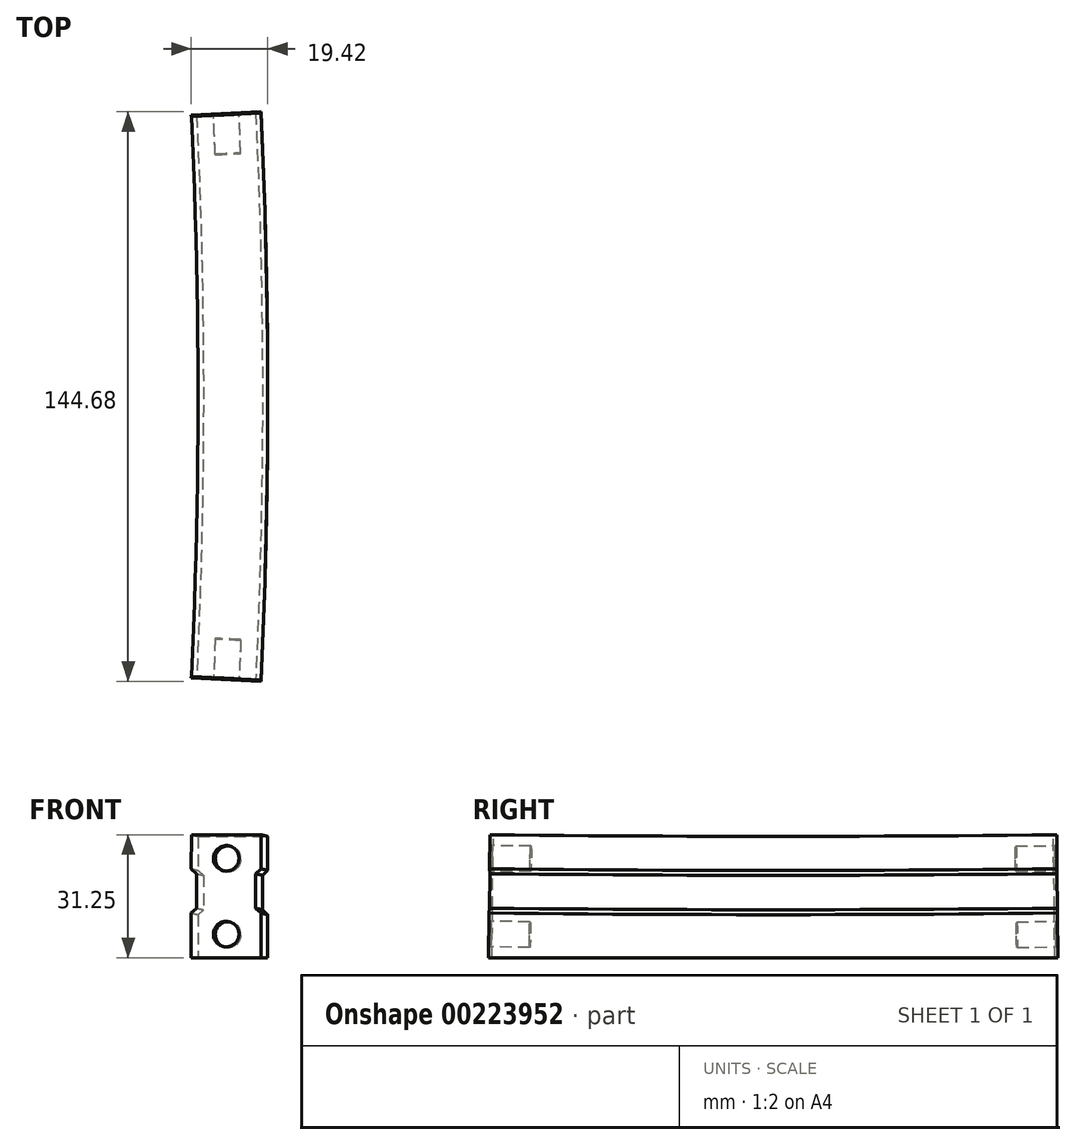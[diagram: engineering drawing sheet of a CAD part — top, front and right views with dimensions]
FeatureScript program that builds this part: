
annotation { "Feature Type Name" : "Feature", "Feature Type Description" : "" }
export const myFeature = defineFeature(function(context is Context, id is Id, definition is map)
    precondition{}
    {
        {
            var Q0;
            Q0=qCreatedBy(makeId("Front.planeOp"),FACE);
            var sketch = newSketch(context, id + "F0", { "sketchPlane" : qUnion([Q0])});
            skLineSegment(sketch, "E0.bottom", {"start": v(0, 0) * mm, "end": v(17.7, 0) * mm, "construction": true});
            skLineSegment(sketch, "E0.top", {"start": v(0, 31.25) * mm, "end": v(17.7, 31.25) * mm, "construction": true});
            skLineSegment(sketch, "E0.left", {"start": v(0, 0) * mm, "end": v(0, 31.25) * mm, "construction": true});
            skLineSegment(sketch, "E0.right", {"start": v(17.7, 0) * mm, "end": v(17.7, 31.25) * mm, "construction": true});
            skLineSegment(sketch, "E1", {"start": v(8.85, 31.25) * mm, "end": v(8.85, 0) * mm, "construction": true});
            skLineSegment(sketch, "E2", {"start": v(8.85, 0) * mm, "end": v(0, 0) * mm});
            skLineSegment(sketch, "E3", {"start": v(0, 11.35) * mm, "end": v(1.35, 12.6) * mm});
            skLineSegment(sketch, "E4", {"start": v(1.35, 12.6) * mm, "end": v(1.35, 21.35) * mm});
            skLineSegment(sketch, "E5", {"start": v(1.35, 21.35) * mm, "end": v(0, 22.6) * mm});
            skLineSegment(sketch, "E6", {"start": v(0, 22.6) * mm, "end": v(0, 31.25) * mm});
            skLineSegment(sketch, "E7", {"start": v(8.85, 31.25) * mm, "end": v(0, 31.25) * mm});
            skLineSegment(sketch, "E8", {"start": v(0, 0) * mm, "end": v(0, 11.35) * mm});
            skLineSegment(sketch, "E9.MirrorCS", {"start": v(16.35, 21.35) * mm, "end": v(17.7, 22.6) * mm});
            skLineSegment(sketch, "E10.MirrorCS", {"start": v(17.7, 11.35) * mm, "end": v(16.35, 12.6) * mm});
            skLineSegment(sketch, "E11.MirrorCS", {"start": v(17.7, 0) * mm, "end": v(17.7, 11.35) * mm});
            skLineSegment(sketch, "E12.MirrorCS", {"start": v(8.85, 31.25) * mm, "end": v(17.7, 31.25) * mm});
            skLineSegment(sketch, "E13.MirrorCS", {"start": v(8.85, 0) * mm, "end": v(17.7, 0) * mm});
            skLineSegment(sketch, "E14.MirrorCS", {"start": v(16.35, 12.6) * mm, "end": v(16.35, 21.35) * mm});
            skLineSegment(sketch, "E15.MirrorCS", {"start": v(17.7, 22.6) * mm, "end": v(17.7, 31.25) * mm});
            skLineSegment(sketch, "E16", {"start": v(0, 11.35) * mm, "end": v(1.35, 11.35) * mm, "construction": true});
            skLineSegment(sketch, "E17", {"start": v(1.35, 11.35) * mm, "end": v(1.35, 12.6) * mm, "construction": true});
            skLineSegment(sketch, "E18", {"start": v(0, 22.6) * mm, "end": v(1.35, 22.6) * mm, "construction": true});
            skLineSegment(sketch, "E19", {"start": v(1.35, 22.6) * mm, "end": v(1.35, 21.35) * mm, "construction": true});
            skPoint(sketch, "E20", {"position": v(17.7, 0) * mm});
            skLineSegment(sketch, "E21", {"start": v(0.24, 33.32) * mm, "end": v(17.46, 29.18) * mm, "construction": true});
            skSolve(sketch);
        }
        {
            var Q0;
            Q0=qCreatedBy(makeId("Top.planeOp"),FACE);
            var Q1;
            Q1=sQuery(id+"F0.wireOp",EDGE,"E21");
            cPlane(context, id + "F1", {"entities" : qUnion([Q0, Q1]), "cplaneType" : CPlaneType.LINE_ANGLE, "offset" : 25 * mm, "angle" : 0 * degree, "width" : 150 * mm, "height" : 150 * mm});
        }
        {
            var Q0;
            Q0=qCreatedBy(id+"F1.planeOp",FACE);
            var sketch = newSketch(context, id + "F2", { "sketchPlane" : qUnion([Q0])});
            skArc(sketch, "E22", {"start": v(1.31, 0) * mm, "mid": v(0.88, 35.79) * mm, "end": v(-0.44, 71.56) * mm});
            skArc(sketch, "E23", {"start": v(1.31, 0) * mm, "mid": v(0.88, -35.79) * mm, "end": v(-0.44, -71.56) * mm});
            skLineSegment(sketch, "E24", {"start": v(-1457.02, 0) * mm, "end": v(1.31, 0) * mm, "construction": true});
            skLineSegment(sketch, "E25", {"start": v(-0.44, 71.56) * mm, "end": v(-1457.02, 0) * mm, "construction": true});
            skLineSegment(sketch, "E26", {"start": v(-0.44, -71.56) * mm, "end": v(-1457.02, 0) * mm, "construction": true});
            skSolve(sketch);
        }
        {
            var Q0;
            Q0 = qSketchRegion(id + "F0", true);
            var Q1;
            Q1=sQuery(id+"F2.wireOp",EDGE,"E22");
            sweep(context, id + "F3", {"profiles" : qUnion([Q0]), "path" : qUnion([Q1])});
        }
        {
            var Q0;
            Q0 = qSketchRegion(id + "F0", true);
            var Q1;
            Q1=sQuery(id+"F2.wireOp",EDGE,"E23");
            sweep(context, id + "F4", {"operationType" : NewBodyOperationType.ADD, "profiles" : qUnion([Q0]), "path" : qUnion([Q1])});
        }
        {
            var Q0;
            Q0=makeQuery(id+"F3.opSweep","CAP_FACE",FACE,{"disambiguationData":[OSD([sQuery(id+"F0.wireOp",EDGE,"E2"),sQuery(id+"F0.wireOp",EDGE,"E3"),sQuery(id+"F0.wireOp",EDGE,"E4"),sQuery(id+"F0.wireOp",EDGE,"E5"),sQuery(id+"F0.wireOp",EDGE,"E6"),sQuery(id+"F0.wireOp",EDGE,"E7"),sQuery(id+"F0.wireOp",EDGE,"E8"),sQuery(id+"F0.wireOp",EDGE,"E9.MirrorCS"),sQuery(id+"F0.wireOp",EDGE,"E10.MirrorCS"),sQuery(id+"F0.wireOp",EDGE,"E11.MirrorCS"),sQuery(id+"F0.wireOp",EDGE,"E12.MirrorCS"),sQuery(id+"F0.wireOp",EDGE,"E13.MirrorCS"),sQuery(id+"F0.wireOp",EDGE,"E14.MirrorCS"),sQuery(id+"F0.wireOp",EDGE,"E15.MirrorCS"),sQuery(id+"F2.wireOp",VERTEX,"E22.end")])],"isStart":false});
            var sketch = newSketch(context, id + "F5", { "sketchPlane" : qUnion([Q0])});
            skLineSegment(sketch, "E27.bottom", {"start": v(1.71, 30.84) * mm, "end": v(19.42, 30.84) * mm, "construction": true});
            skLineSegment(sketch, "E27.top", {"start": v(1.71, -0.41) * mm, "end": v(19.42, -0.41) * mm, "construction": true});
            skLineSegment(sketch, "E27.left", {"start": v(1.71, 30.84) * mm, "end": v(1.71, -0.41) * mm, "construction": true});
            skLineSegment(sketch, "E27.right", {"start": v(19.42, 30.84) * mm, "end": v(19.42, -0.41) * mm, "construction": true});
            skLineSegment(sketch, "E28", {"start": v(10.57, 30.84) * mm, "end": v(10.57, -0.41) * mm, "construction": true});
            skCircle(sketch, "E29", {"center": v(10.57, 5.59) * mm, "radius": 3.25 * mm});
            skCircle(sketch, "E30", {"center": v(10.57, 24.84) * mm, "radius": 3.25 * mm});
            skSolve(sketch);
        }
        {
            var Q0;
            Q0=makeQuery(id+"F5.imprint","IMPRINT",FACE,{"disambiguationData":[TD([[makeQuery(id+"F5.imprint","IMPRINT",EDGE,{"derivedFrom":sQuery(id+"F5.wireOp",EDGE,"E30")}),1.0]])]});
            var Q1;
            Q1=makeQuery(id+"F5.imprint","IMPRINT",FACE,{"disambiguationData":[TD([[makeQuery(id+"F5.imprint","IMPRINT",EDGE,{"derivedFrom":sQuery(id+"F5.wireOp",EDGE,"E29")}),1.0]])]});
            extrude(context, id + "F6", {"entities" : qUnion([Q0, Q1]), "operationType" : NewBodyOperationType.REMOVE, "oppositeDirection" : true, "depth" : 10 * mm});
        }
        {
            var Q0;
            Q0=makeQuery(id+"F4.opSweep","CAP_FACE",FACE,{"disambiguationData":[OSD([sQuery(id+"F0.wireOp",EDGE,"E2"),sQuery(id+"F0.wireOp",EDGE,"E3"),sQuery(id+"F0.wireOp",EDGE,"E4"),sQuery(id+"F0.wireOp",EDGE,"E5"),sQuery(id+"F0.wireOp",EDGE,"E6"),sQuery(id+"F0.wireOp",EDGE,"E7"),sQuery(id+"F0.wireOp",EDGE,"E8"),sQuery(id+"F0.wireOp",EDGE,"E9.MirrorCS"),sQuery(id+"F0.wireOp",EDGE,"E10.MirrorCS"),sQuery(id+"F0.wireOp",EDGE,"E11.MirrorCS"),sQuery(id+"F0.wireOp",EDGE,"E12.MirrorCS"),sQuery(id+"F0.wireOp",EDGE,"E13.MirrorCS"),sQuery(id+"F0.wireOp",EDGE,"E14.MirrorCS"),sQuery(id+"F0.wireOp",EDGE,"E15.MirrorCS"),sQuery(id+"F2.wireOp",VERTEX,"E23.end")])],"isStart":false});
            var sketch = newSketch(context, id + "F7", { "sketchPlane" : qUnion([Q0])});
            skLineSegment(sketch, "E31.bottom", {"start": v(-19.42, 30.83) * mm, "end": v(-1.71, 30.84) * mm, "construction": true});
            skLineSegment(sketch, "E31.top", {"start": v(-19.42, 32.96) * mm, "end": v(-1.72, 32.97) * mm, "construction": true});
            skLineSegment(sketch, "E31.left", {"start": v(-19.42, 32.96) * mm, "end": v(-19.42, 30.83) * mm, "construction": true});
            skLineSegment(sketch, "E31.right", {"start": v(-1.72, 32.97) * mm, "end": v(-1.71, 30.84) * mm, "construction": true});
            skLineSegment(sketch, "E32", {"start": v(-10.57, 32.96) * mm, "end": v(-10.57, 30.84) * mm, "construction": true});
            skCircle(sketch, "E33", {"center": v(-10.56, 5.59) * mm, "radius": 3.25 * mm});
            skCircle(sketch, "E34", {"center": v(-10.57, 24.84) * mm, "radius": 3.25 * mm});
            skSolve(sketch);
        }
        {
            var Q0;
            Q0 = qSketchRegion(id + "F7", true);
            extrude(context, id + "F8", {"entities" : qUnion([Q0]), "operationType" : NewBodyOperationType.REMOVE, "oppositeDirection" : true, "depth" : 10 * mm});
        }
        {
            var Q0;
            Q0=qCreatedBy(makeId("Top.planeOp"),FACE);
            var sketch = newSketch(context, id + "F9", { "sketchPlane" : qUnion([Q0])});
            skLineSegment(sketch, "E35.bottom", {"start": v(22.42, 84.98) * mm, "end": v(-22.42, 84.98) * mm});
            skLineSegment(sketch, "E35.top", {"start": v(22.42, -84.98) * mm, "end": v(-22.42, -84.98) * mm});
            skLineSegment(sketch, "E35.left", {"start": v(22.42, 84.98) * mm, "end": v(22.42, -84.98) * mm});
            skLineSegment(sketch, "E35.right", {"start": v(-22.42, 84.98) * mm, "end": v(-22.42, -84.98) * mm});
            skPoint(sketch, "E35.middle", {"position": v(0, 0) * mm});
            skSolve(sketch);
        }
        {
            var Q0;
            Q0 = qSketchRegion(id + "F9", true);
            var Q1;
            Q1=makeQuery(id+"F3.opSweep","CAP_VERTEX",VERTEX,{"disambiguationData":[OSD([sQuery(id+"F0.wireOp",EDGE,"E11.MirrorCS"),sQuery(id+"F0.wireOp",EDGE,"E13.MirrorCS"),sQuery(id+"F2.wireOp",EDGE,"E22")])],"isStart":false});
            extrude(context, id + "F10", {"entities" : qUnion([Q0]), "operationType" : NewBodyOperationType.REMOVE, "endBound" : BoundingType.UP_TO_VERTEX, "endBoundEntityVertex" : qUnion([Q1]), "depth" : 25 * mm});
        }
    });
